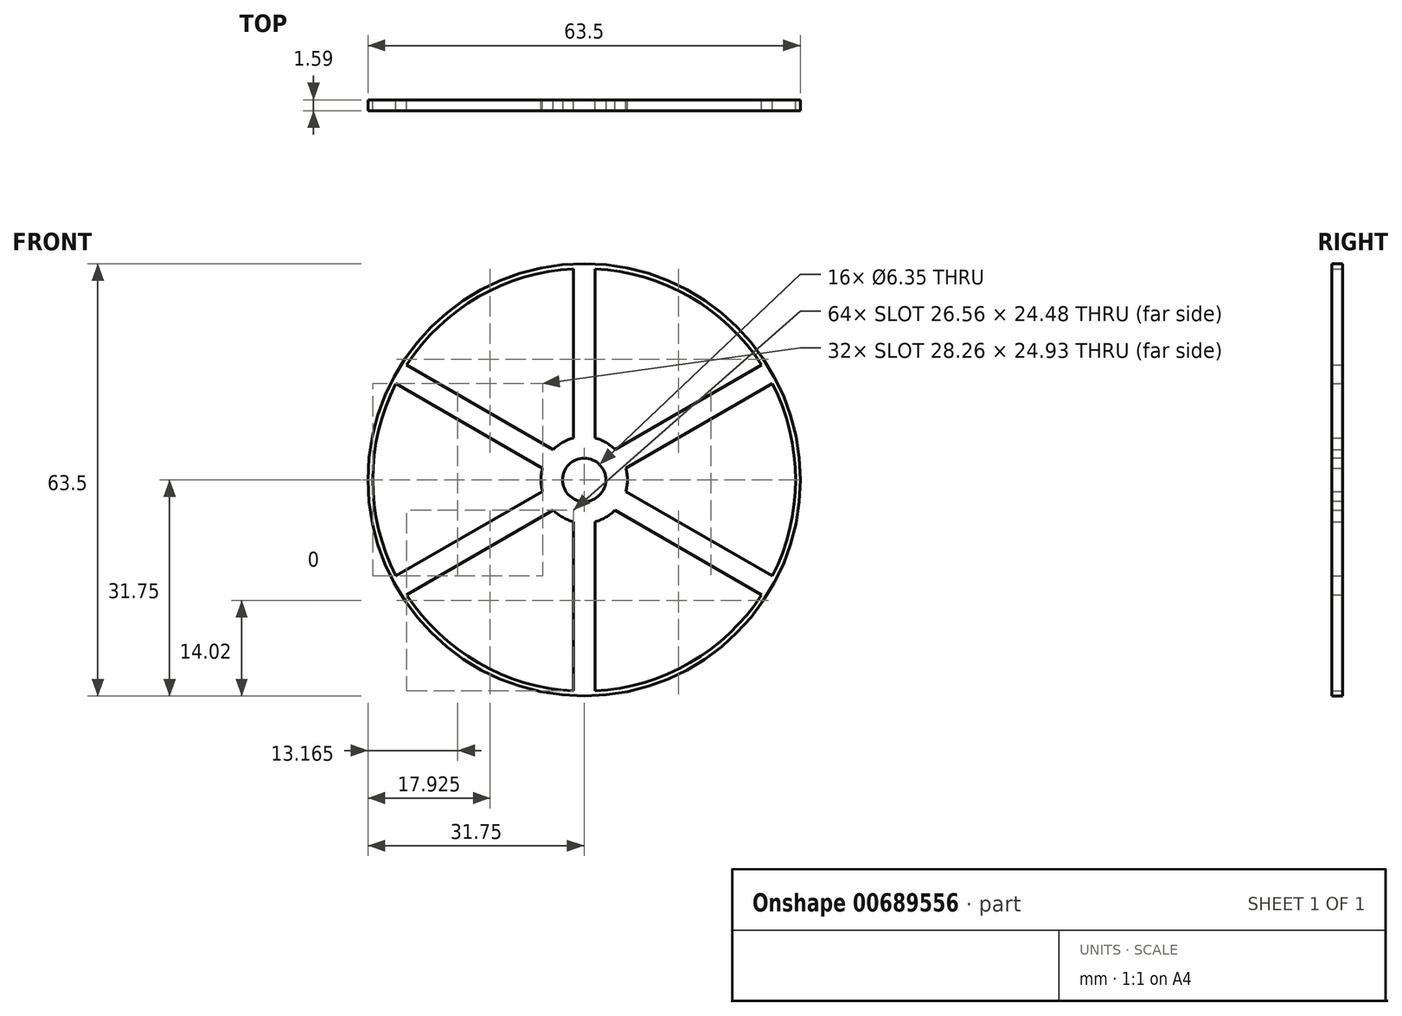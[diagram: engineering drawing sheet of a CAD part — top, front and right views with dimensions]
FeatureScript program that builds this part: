
annotation { "Feature Type Name" : "Feature", "Feature Type Description" : "" }
export const myFeature = defineFeature(function(context is Context, id is Id, definition is map)
    precondition{}
    {
        {
            var Q0;
            Q0=qCreatedBy(makeId("Front.planeOp"),FACE);
            var sketch = newSketch(context, id + "F0", { "sketchPlane" : qUnion([Q0])});
            skArc(sketch, "E0", {"start": v(-1.59, 31.01) * mm, "mid": v(-15.53, 26.9) * mm, "end": v(-26.06, 16.88) * mm});
            skCircle(sketch, "E1", {"center": v(0, 0) * mm, "radius": 31.75 * mm});
            skArc(sketch, "E2", {"start": v(-4.53, -4.45) * mm, "mid": v(-3.17, -5.5) * mm, "end": v(-1.59, -6.15) * mm});
            skLineSegment(sketch, "E3.trimOffspring", {"start": v(-1.59, 6.15) * mm, "end": v(-1.59, 31.05) * mm});
            skLineSegment(sketch, "E4.trimOffspring", {"start": v(1.59, 6.15) * mm, "end": v(1.59, 31.05) * mm});
            skLineSegment(sketch, "E5.trimOffspring", {"start": v(4.53, 4.45) * mm, "end": v(26.1, 16.9) * mm});
            skLineSegment(sketch, "E6.trimOffspring", {"start": v(6.12, 1.7) * mm, "end": v(27.69, 14.15) * mm});
            skLineSegment(sketch, "E7.trimOffspring", {"start": v(6.12, -1.7) * mm, "end": v(27.69, -14.15) * mm});
            skLineSegment(sketch, "E8.trimOffspring", {"start": v(4.53, -4.45) * mm, "end": v(26.1, -16.9) * mm});
            skLineSegment(sketch, "E9.trimOffspring", {"start": v(1.59, -6.15) * mm, "end": v(1.59, -31.05) * mm});
            skLineSegment(sketch, "E10.trimOffspring", {"start": v(-1.59, -6.15) * mm, "end": v(-1.59, -31.05) * mm});
            skLineSegment(sketch, "E11.trimOffspring", {"start": v(-4.53, -4.45) * mm, "end": v(-26.1, -16.9) * mm});
            skLineSegment(sketch, "E12.trimOffspring", {"start": v(-6.12, -1.7) * mm, "end": v(-27.69, -14.15) * mm});
            skArc(sketch, "E13.trimOffspring", {"start": v(-6.12, 1.7) * mm, "mid": v(-6.35, 0) * mm, "end": v(-6.12, -1.7) * mm});
            skArc(sketch, "E14.trimOffspring", {"start": v(-1.59, 6.15) * mm, "mid": v(-3.17, 5.5) * mm, "end": v(-4.53, 4.45) * mm});
            skArc(sketch, "E15.trimOffspring", {"start": v(4.53, 4.45) * mm, "mid": v(3.18, 5.5) * mm, "end": v(1.59, 6.15) * mm});
            skArc(sketch, "E16.trimOffspring", {"start": v(6.12, -1.7) * mm, "mid": v(6.35, 0) * mm, "end": v(6.12, 1.7) * mm});
            skArc(sketch, "E17.trimOffspring", {"start": v(1.59, -6.15) * mm, "mid": v(3.17, -5.5) * mm, "end": v(4.53, -4.45) * mm});
            skArc(sketch, "E18.trimOffspring", {"start": v(26.06, 16.88) * mm, "mid": v(15.53, 26.9) * mm, "end": v(1.59, 31.01) * mm});
            skArc(sketch, "E19.trimOffspring", {"start": v(27.65, -14.13) * mm, "mid": v(31.05, 0) * mm, "end": v(27.65, 14.13) * mm});
            skArc(sketch, "E20.trimOffspring", {"start": v(-27.65, 14.13) * mm, "mid": v(-31.05, 0) * mm, "end": v(-27.65, -14.13) * mm});
            skArc(sketch, "E21.trimOffspring", {"start": v(-26.06, -16.88) * mm, "mid": v(-15.53, -26.9) * mm, "end": v(-1.59, -31.01) * mm});
            skArc(sketch, "E22.trimOffspring", {"start": v(1.59, -31.01) * mm, "mid": v(15.53, -26.9) * mm, "end": v(26.06, -16.88) * mm});
            skLineSegment(sketch, "E23.trimOffspring", {"start": v(-4.53, 4.45) * mm, "end": v(-26.1, 16.9) * mm});
            skLineSegment(sketch, "E24.trimOffspring", {"start": v(-6.12, 1.7) * mm, "end": v(-27.69, 14.15) * mm});
            skSolve(sketch);
        }
        {
            var Q0;
            Q0 = qSketchRegion(id + "F0", true);
            extrude(context, id + "F1", {"entities" : qUnion([Q0]), "depth" : 1.59 * mm, "offsetDistance" : 25.4 * mm});
        }
        {
            var Q0;
            Q0=makeQuery(id+"F1.opExtrude","CAP_FACE",FACE,{"disambiguationData":[OSD([sQuery(id+"F0.wireOp",EDGE,"E0"),sQuery(id+"F0.wireOp",EDGE,"E1"),sQuery(id+"F0.wireOp",EDGE,"E2"),sQuery(id+"F0.wireOp",EDGE,"E3.trimOffspring"),sQuery(id+"F0.wireOp",EDGE,"E4.trimOffspring"),sQuery(id+"F0.wireOp",EDGE,"E5.trimOffspring"),sQuery(id+"F0.wireOp",EDGE,"E6.trimOffspring"),sQuery(id+"F0.wireOp",EDGE,"E7.trimOffspring"),sQuery(id+"F0.wireOp",EDGE,"E8.trimOffspring"),sQuery(id+"F0.wireOp",EDGE,"E9.trimOffspring"),sQuery(id+"F0.wireOp",EDGE,"E10.trimOffspring"),sQuery(id+"F0.wireOp",EDGE,"E11.trimOffspring"),sQuery(id+"F0.wireOp",EDGE,"E12.trimOffspring"),sQuery(id+"F0.wireOp",EDGE,"E13.trimOffspring"),sQuery(id+"F0.wireOp",EDGE,"E14.trimOffspring"),sQuery(id+"F0.wireOp",EDGE,"E15.trimOffspring"),sQuery(id+"F0.wireOp",EDGE,"E16.trimOffspring"),sQuery(id+"F0.wireOp",EDGE,"E17.trimOffspring"),sQuery(id+"F0.wireOp",EDGE,"E18.trimOffspring"),sQuery(id+"F0.wireOp",EDGE,"E19.trimOffspring"),sQuery(id+"F0.wireOp",EDGE,"E20.trimOffspring"),sQuery(id+"F0.wireOp",EDGE,"E21.trimOffspring"),sQuery(id+"F0.wireOp",EDGE,"E22.trimOffspring"),sQuery(id+"F0.wireOp",EDGE,"E23.trimOffspring"),sQuery(id+"F0.wireOp",EDGE,"E24.trimOffspring")])],"isStart":false});
            var sketch = newSketch(context, id + "F2", { "sketchPlane" : qUnion([Q0])});
            skCircle(sketch, "E25", {"center": v(0, 0) * mm, "radius": 3.18 * mm});
            skSolve(sketch);
        }
        {
            var Q0;
            Q0 = qSketchRegion(id + "F2", true);
            extrude(context, id + "F3", {"entities" : qUnion([Q0]), "operationType" : NewBodyOperationType.REMOVE, "oppositeDirection" : true, "depth" : 25.4 * mm, "offsetDistance" : 25.4 * mm});
        }
    });
